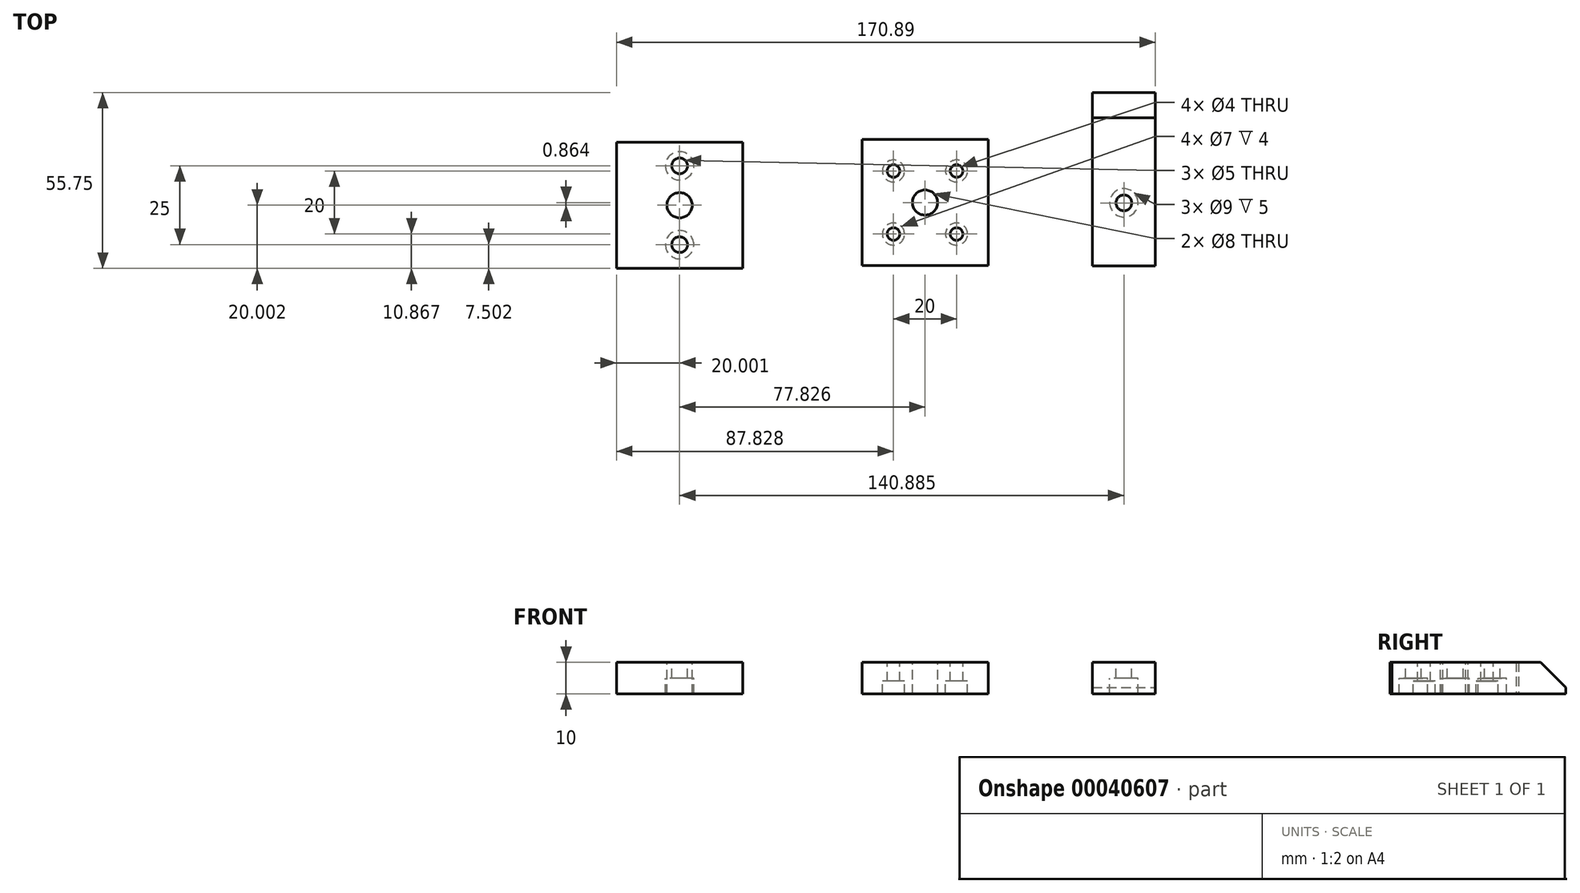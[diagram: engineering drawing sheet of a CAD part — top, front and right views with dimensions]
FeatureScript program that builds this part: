
annotation { "Feature Type Name" : "Feature", "Feature Type Description" : "" }
export const myFeature = defineFeature(function(context is Context, id is Id, definition is map)
    precondition{}
    {
        {
            var Q0;
            Q0=qCreatedBy(makeId("Top.planeOp"),FACE);
            var sketch = newSketch(context, id + "F0", { "sketchPlane" : qUnion([Q0])});
            skLineSegment(sketch, "E0.bottom", {"start": v(-23.11, -14.65) * mm, "end": v(16.89, -14.65) * mm});
            skLineSegment(sketch, "E0.top", {"start": v(-23.11, 25.35) * mm, "end": v(16.89, 25.35) * mm});
            skLineSegment(sketch, "E0.left", {"start": v(-23.11, -14.65) * mm, "end": v(-23.11, 25.35) * mm});
            skLineSegment(sketch, "E0.right", {"start": v(16.89, -14.65) * mm, "end": v(16.89, 25.35) * mm});
            skLineSegment(sketch, "E1.bottom", {"start": v(49.95, -14.77) * mm, "end": v(69.95, -14.77) * mm});
            skLineSegment(sketch, "E1.top", {"start": v(49.95, 40.23) * mm, "end": v(69.95, 40.23) * mm});
            skLineSegment(sketch, "E1.left", {"start": v(49.95, -14.77) * mm, "end": v(49.95, 40.23) * mm});
            skLineSegment(sketch, "E1.right", {"start": v(69.95, -14.77) * mm, "end": v(69.95, 40.23) * mm});
            skPoint(sketch, "E2", {"position": v(59.95, 5.23) * mm});
            skLineSegment(sketch, "E3", {"start": v(-23.11, 5.35) * mm, "end": v(16.89, 5.35) * mm, "construction": true});
            skLineSegment(sketch, "E4", {"start": v(-23.11, 15.35) * mm, "end": v(16.89, 15.35) * mm, "construction": true});
            skLineSegment(sketch, "E5", {"start": v(-23.11, -4.65) * mm, "end": v(16.89, -4.65) * mm, "construction": true});
            skLineSegment(sketch, "E6", {"start": v(-3.11, 25.35) * mm, "end": v(-3.11, -14.65) * mm, "construction": true});
            skLineSegment(sketch, "E7", {"start": v(-13.11, 25.35) * mm, "end": v(-13.11, -14.65) * mm, "construction": true});
            skLineSegment(sketch, "E8", {"start": v(6.89, 25.35) * mm, "end": v(6.89, -14.65) * mm, "construction": true});
            skLineSegment(sketch, "E9.bottom", {"start": v(-60.94, -15.52) * mm, "end": v(-100.94, -15.52) * mm});
            skLineSegment(sketch, "E9.top", {"start": v(-60.94, 24.48) * mm, "end": v(-100.94, 24.48) * mm});
            skLineSegment(sketch, "E9.left", {"start": v(-60.94, -15.52) * mm, "end": v(-60.94, 24.48) * mm});
            skLineSegment(sketch, "E9.right", {"start": v(-100.94, -15.52) * mm, "end": v(-100.94, 24.48) * mm});
            skLineSegment(sketch, "E10", {"start": v(-80.94, 24.48) * mm, "end": v(-80.94, -15.52) * mm, "construction": true});
            skPoint(sketch, "E11", {"position": v(-80.94, 4.48) * mm});
            skPoint(sketch, "E12", {"position": v(-80.94, 16.98) * mm});
            skPoint(sketch, "E13", {"position": v(-80.94, -8.02) * mm});
            skLineSegment(sketch, "E14", {"start": v(-100.94, 4.48) * mm, "end": v(-60.94, 4.48) * mm, "construction": true});
            skPoint(sketch, "E15", {"position": v(-13.11, 15.35) * mm});
            skPoint(sketch, "E16", {"position": v(-13.11, -4.65) * mm});
            skPoint(sketch, "E17", {"position": v(6.89, -4.65) * mm});
            skPoint(sketch, "E18", {"position": v(6.89, 15.35) * mm});
            skPoint(sketch, "E19", {"position": v(-3.11, 5.35) * mm});
            skSolve(sketch);
        }
        {
            var Q0;
            Q0=makeQuery(id+"F0.imprint","IMPRINT",FACE,{"disambiguationData":[TD([[makeQuery(id+"F0.imprint","IMPRINT",EDGE,{"derivedFrom":sQuery(id+"F0.wireOp",EDGE,"E9.bottom")}),-1.0]])]});
            var Q1;
            Q1=makeQuery(id+"F0.imprint","IMPRINT",FACE,{"disambiguationData":[TD([[makeQuery(id+"F0.imprint","IMPRINT",EDGE,{"derivedFrom":sQuery(id+"F0.wireOp",EDGE,"E0.bottom")}),1.0]])]});
            var Q2;
            Q2=makeQuery(id+"F0.imprint","IMPRINT",FACE,{"disambiguationData":[TD([[makeQuery(id+"F0.imprint","IMPRINT",EDGE,{"derivedFrom":sQuery(id+"F0.wireOp",EDGE,"E1.bottom")}),1.0]])]});
            extrude(context, id + "F1", {"entities" : qUnion([Q0, Q1, Q2]), "depth" : 10 * mm});
        }
        {
            var Q0;
            Q0=sQuery(id+"F0.wireOp",VERTEX,"E19");
            var Q1;
            Q1=sQuery(id+"F0.wireOp",VERTEX,"E11");
            var Q2;
            Q2=makeQuery(id+"F1.opExtrude","SWEPT_BODY",BODY,{"disambiguationData":[OSD([sQuery(id+"F0.wireOp",EDGE,"E0.bottom"),sQuery(id+"F0.wireOp",EDGE,"E0.top"),sQuery(id+"F0.wireOp",EDGE,"E0.left"),sQuery(id+"F0.wireOp",EDGE,"E0.right")])]});
            var Q3;
            Q3=makeQuery(id+"F1.opExtrude","SWEPT_BODY",BODY,{"disambiguationData":[OSD([sQuery(id+"F0.wireOp",EDGE,"E9.bottom"),sQuery(id+"F0.wireOp",EDGE,"E9.top"),sQuery(id+"F0.wireOp",EDGE,"E9.left"),sQuery(id+"F0.wireOp",EDGE,"E9.right")])]});
            hole(context, id + "F2", {"style" : HoleStyle.SIMPLE, "endStyle" : HoleEndStyle.THROUGH, "oppositeDirection" : true, "holeDiameter" : 8 * mm, "tappedDepth" : 12 * mm, "tapClearance" : 3, "locations" : qUnion([Q0, Q1]), "scope" : qUnion([Q2, Q3])});
        }
        {
            var Q0;
            Q0=sQuery(id+"F0.wireOp",VERTEX,"E18");
            var Q1;
            Q1=sQuery(id+"F0.wireOp",VERTEX,"E15");
            var Q2;
            Q2=sQuery(id+"F0.wireOp",VERTEX,"E16");
            var Q3;
            Q3=sQuery(id+"F0.wireOp",VERTEX,"E17");
            var Q4;
            Q4=makeQuery(id+"F1.opExtrude","SWEPT_BODY",BODY,{"disambiguationData":[OSD([sQuery(id+"F0.wireOp",EDGE,"E0.bottom"),sQuery(id+"F0.wireOp",EDGE,"E0.top"),sQuery(id+"F0.wireOp",EDGE,"E0.left"),sQuery(id+"F0.wireOp",EDGE,"E0.right")])]});
            hole(context, id + "F3", {"style" : HoleStyle.C_BORE, "endStyle" : HoleEndStyle.THROUGH, "oppositeDirection" : true, "holeDiameter" : 4 * mm, "cBoreDiameter" : 7 * mm, "cBoreDepth" : 4 * mm, "tappedDepth" : 12 * mm, "tapClearance" : 3, "locations" : qUnion([Q0, Q1, Q2, Q3]), "scope" : qUnion([Q4])});
        }
        {
            var Q0;
            Q0=sQuery(id+"F0.wireOp",VERTEX,"E2");
            var Q1;
            Q1=sQuery(id+"F0.wireOp",VERTEX,"E12");
            var Q2;
            Q2=sQuery(id+"F0.wireOp",VERTEX,"E13");
            var Q3;
            Q3=makeQuery(id+"F1.opExtrude","SWEPT_BODY",BODY,{"disambiguationData":[OSD([sQuery(id+"F0.wireOp",EDGE,"E9.bottom"),sQuery(id+"F0.wireOp",EDGE,"E9.top"),sQuery(id+"F0.wireOp",EDGE,"E9.left"),sQuery(id+"F0.wireOp",EDGE,"E9.right")])]});
            var Q4;
            Q4=makeQuery(id+"F1.opExtrude","SWEPT_BODY",BODY,{"disambiguationData":[OSD([sQuery(id+"F0.wireOp",EDGE,"E1.bottom"),sQuery(id+"F0.wireOp",EDGE,"E1.top"),sQuery(id+"F0.wireOp",EDGE,"E1.left"),sQuery(id+"F0.wireOp",EDGE,"E1.right")])]});
            hole(context, id + "F4", {"style" : HoleStyle.C_BORE, "endStyle" : HoleEndStyle.THROUGH, "oppositeDirection" : true, "holeDiameter" : 5 * mm, "cBoreDiameter" : 9 * mm, "cBoreDepth" : 5 * mm, "tappedDepth" : 12 * mm, "tapClearance" : 3, "locations" : qUnion([Q0, Q1, Q2]), "scope" : qUnion([Q3, Q4])});
        }
        {
            var Q0;
            Q0=makeQuery(id+"F1.opExtrude","CAP_EDGE",EDGE,{"disambiguationData":[OSD([sQuery(id+"F0.wireOp",EDGE,"E1.top")])],"isStart":false});
            chamfer(context, id + "F5", {"entities" : qUnion([Q0]), "width" : 8 * mm, "tangentPropagation" : true});
        }
    });
